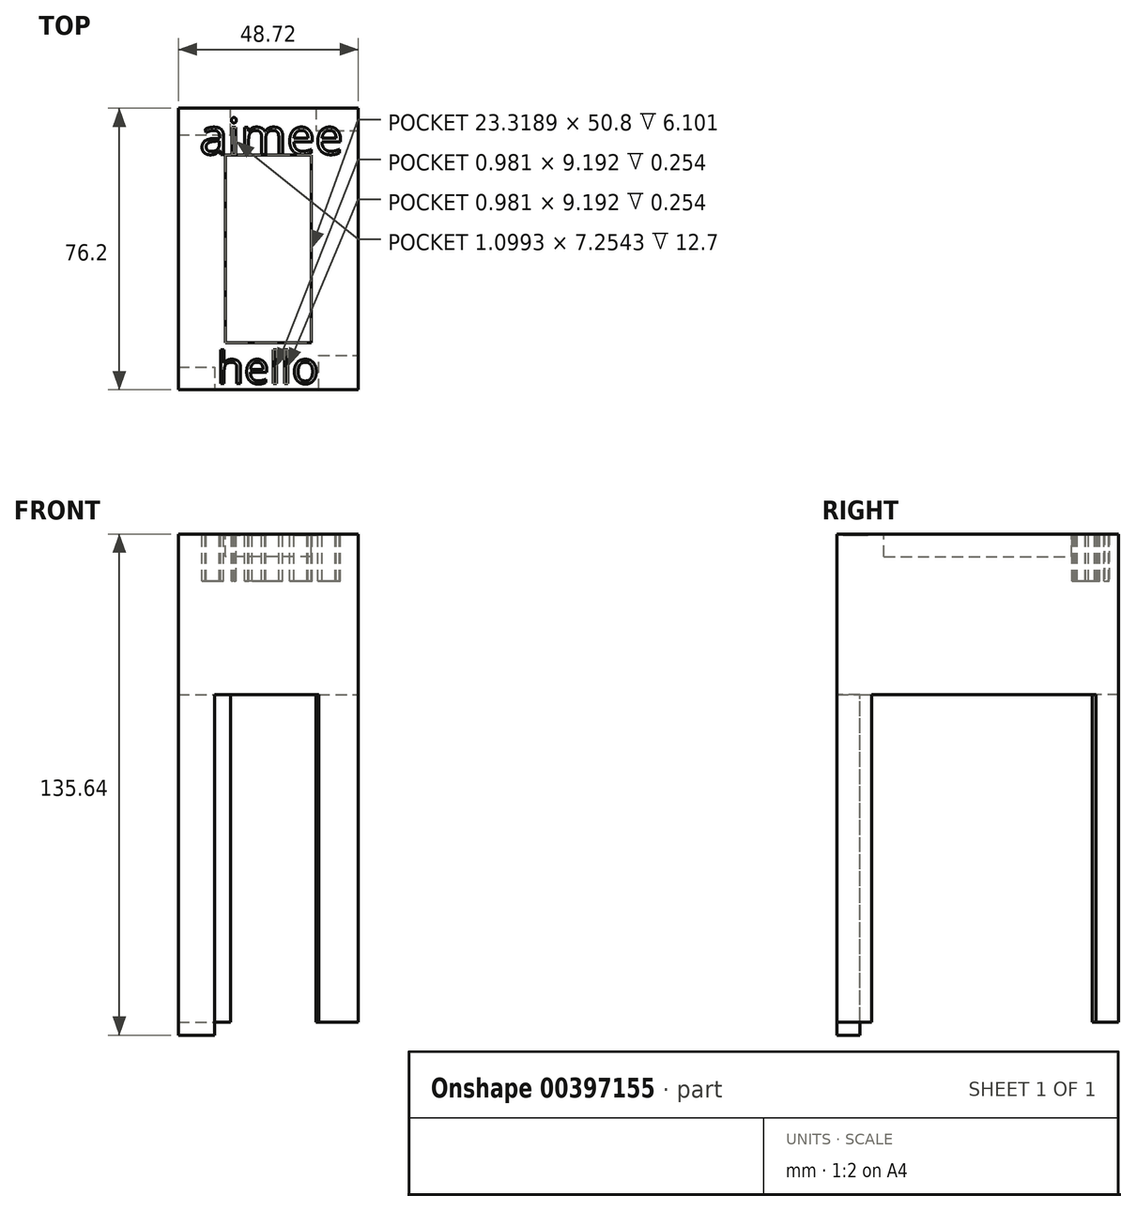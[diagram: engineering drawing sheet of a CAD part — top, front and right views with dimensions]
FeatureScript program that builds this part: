
annotation { "Feature Type Name" : "Feature", "Feature Type Description" : "" }
export const myFeature = defineFeature(function(context is Context, id is Id, definition is map)
    precondition{}
    {
        {
            var Q0;
            Q0=qCreatedBy(makeId("Front.planeOp"),FACE);
            var sketch = newSketch(context, id + "F0", { "sketchPlane" : qUnion([Q0])});
            skLineSegment(sketch, "E0.bottom", {"start": v(-31.88, 2.44) * mm, "end": v(16.84, 2.44) * mm});
            skLineSegment(sketch, "E0.top", {"start": v(-31.88, 45.88) * mm, "end": v(16.84, 45.88) * mm});
            skLineSegment(sketch, "E0.left", {"start": v(-31.88, 2.44) * mm, "end": v(-31.88, 45.88) * mm});
            skLineSegment(sketch, "E0.right", {"start": v(16.84, 2.44) * mm, "end": v(16.84, 45.88) * mm});
            skSolve(sketch);
        }
        {
            var Q0;
            Q0=makeQuery(id+"F0.imprint","IMPRINT",FACE,{"disambiguationData":[TD([[makeQuery(id+"F0.imprint","IMPRINT",EDGE,{"derivedFrom":sQuery(id+"F0.wireOp",EDGE,"E0.bottom")}),1.0]])]});
            extrude(context, id + "F1", {"entities" : qUnion([Q0]), "depth" : 76.2 * mm});
        }
        {
            var Q0;
            Q0=makeQuery(id+"F1.opExtrude","SWEPT_FACE",FACE,{"disambiguationData":[OSD([sQuery(id+"F0.wireOp",EDGE,"E0.top")])]});
            shell(context, id + "F2", {"entities" : qUnion([Q0]), "thickness" : 12.7 * mm});
        }
        {
            var Q0;
            Q0=makeQuery(id+"F1.opExtrude","CAP_FACE",FACE,{"disambiguationData":[OSD([sQuery(id+"F0.wireOp",EDGE,"E0.bottom"),sQuery(id+"F0.wireOp",EDGE,"E0.top"),sQuery(id+"F0.wireOp",EDGE,"E0.left"),sQuery(id+"F0.wireOp",EDGE,"E0.right")])],"isStart":false});
            var Q1;
            Q1=makeQuery(id+"F1.opExtrude","SWEPT_FACE",FACE,{"disambiguationData":[OSD([sQuery(id+"F0.wireOp",EDGE,"E0.right")])]});
            var Q2;
            Q2=makeQuery(id+"F1.opExtrude","SWEPT_FACE",FACE,{"disambiguationData":[OSD([sQuery(id+"F0.wireOp",EDGE,"E0.left")])]});
            shell(context, id + "F3", {"entities" : qUnion([Q0, Q1, Q2]), "thickness" : 2.54 * mm});
        }
        {
            var Q0;
            Q0=makeQuery(id+"F1.opExtrude","SWEPT_FACE",FACE,{"disambiguationData":[OSD([sQuery(id+"F0.wireOp",EDGE,"E0.bottom")])]});
            var sketch = newSketch(context, id + "F4", { "sketchPlane" : qUnion([Q0])});
            skLineSegment(sketch, "E1.bottom", {"start": v(-31.88, 69.99) * mm, "end": v(-22.12, 69.99) * mm});
            skLineSegment(sketch, "E1.top", {"start": v(-31.88, 76.2) * mm, "end": v(-22.12, 76.2) * mm});
            skLineSegment(sketch, "E1.left", {"start": v(-31.88, 69.99) * mm, "end": v(-31.88, 76.2) * mm});
            skLineSegment(sketch, "E1.right", {"start": v(-22.12, 69.99) * mm, "end": v(-22.12, 76.2) * mm});
            skSolve(sketch);
        }
        {
            var Q0;
            Q0=makeQuery(id+"F4.imprint","IMPRINT",FACE,{"disambiguationData":[TD([[makeQuery(id+"F4.imprint","IMPRINT",EDGE,{"derivedFrom":sQuery(id+"F4.wireOp",EDGE,"E1.bottom")}),1.0]])]});
            extrude(context, id + "F5", {"entities" : qUnion([Q0]), "operationType" : NewBodyOperationType.ADD, "depth" : 92.2 * mm});
        }
        {
            var Q0;
            Q0=makeQuery(id+"F1.opExtrude","SWEPT_FACE",FACE,{"disambiguationData":[OSD([sQuery(id+"F0.wireOp",EDGE,"E0.bottom")])]});
            var sketch = newSketch(context, id + "F6", { "sketchPlane" : qUnion([Q0])});
            skLineSegment(sketch, "E2.bottom", {"start": v(6.1, 76.2) * mm, "end": v(16.84, 76.2) * mm});
            skLineSegment(sketch, "E2.top", {"start": v(6.1, 66.82) * mm, "end": v(16.84, 66.82) * mm});
            skLineSegment(sketch, "E2.left", {"start": v(6.1, 76.2) * mm, "end": v(6.1, 66.82) * mm});
            skLineSegment(sketch, "E2.right", {"start": v(16.84, 76.2) * mm, "end": v(16.84, 66.82) * mm});
            skSolve(sketch);
        }
        {
            var Q0;
            Q0=makeQuery(id+"F6.imprint","IMPRINT",FACE,{"disambiguationData":[TD([[makeQuery(id+"F6.imprint","IMPRINT",EDGE,{"derivedFrom":sQuery(id+"F6.wireOp",EDGE,"E2.bottom")}),-1.0]])]});
            extrude(context, id + "F7", {"entities" : qUnion([Q0]), "operationType" : NewBodyOperationType.ADD, "depth" : 88.65 * mm});
        }
        {
            var Q0;
            Q0=makeQuery(id+"F1.opExtrude","SWEPT_FACE",FACE,{"disambiguationData":[OSD([sQuery(id+"F0.wireOp",EDGE,"E0.bottom")])]});
            var sketch = newSketch(context, id + "F8", { "sketchPlane" : qUnion([Q0])});
            skLineSegment(sketch, "E3.bottom", {"start": v(-31.88, 7.16) * mm, "end": v(-17.79, 7.16) * mm});
            skLineSegment(sketch, "E3.top", {"start": v(-31.88, 0) * mm, "end": v(-17.79, 0) * mm});
            skLineSegment(sketch, "E3.left", {"start": v(-31.88, 7.16) * mm, "end": v(-31.88, 0) * mm});
            skLineSegment(sketch, "E3.right", {"start": v(-17.79, 7.16) * mm, "end": v(-17.79, 0) * mm});
            skLineSegment(sketch, "E4.bottom", {"start": v(5.33, 0) * mm, "end": v(16.84, 0) * mm});
            skLineSegment(sketch, "E4.top", {"start": v(5.33, 6.1) * mm, "end": v(16.84, 6.1) * mm});
            skLineSegment(sketch, "E4.left", {"start": v(5.33, 0) * mm, "end": v(5.33, 6.1) * mm});
            skLineSegment(sketch, "E4.right", {"start": v(16.84, 0) * mm, "end": v(16.84, 6.1) * mm});
            skSolve(sketch);
        }
        {
            var Q0;
            Q0=makeQuery(id+"F8.imprint","IMPRINT",FACE,{"disambiguationData":[TD([[makeQuery(id+"F8.imprint","IMPRINT",EDGE,{"derivedFrom":sQuery(id+"F8.wireOp",EDGE,"E3.bottom")}),-1.0]])]});
            var Q1;
            Q1=makeQuery(id+"F8.imprint","IMPRINT",FACE,{"disambiguationData":[TD([[makeQuery(id+"F8.imprint","IMPRINT",EDGE,{"derivedFrom":sQuery(id+"F8.wireOp",EDGE,"E4.bottom")}),1.0]])]});
            extrude(context, id + "F9", {"entities" : qUnion([Q0, Q1]), "operationType" : NewBodyOperationType.ADD, "depth" : 56.4 * mm});
        }
        {
            var Q0;
            Q0=makeQuery(id+"F9.opExtrude","CAP_FACE",FACE,{"disambiguationData":[OSD([sQuery(id+"F8.wireOp",EDGE,"E3.bottom"),sQuery(id+"F8.wireOp",EDGE,"E3.top"),sQuery(id+"F8.wireOp",EDGE,"E3.left"),sQuery(id+"F8.wireOp",EDGE,"E3.right")])],"isStart":false});
            var Q1;
            Q1=makeQuery(id+"F9.opExtrude","CAP_FACE",FACE,{"disambiguationData":[OSD([sQuery(id+"F8.wireOp",EDGE,"E4.bottom"),sQuery(id+"F8.wireOp",EDGE,"E4.top"),sQuery(id+"F8.wireOp",EDGE,"E4.left"),sQuery(id+"F8.wireOp",EDGE,"E4.right")])],"isStart":false});
            var Q2;
            Q2=makeQuery(id+"F7.opExtrude","CAP_FACE",FACE,{"disambiguationData":[OSD([sQuery(id+"F6.wireOp",EDGE,"E2.bottom"),sQuery(id+"F6.wireOp",EDGE,"E2.top"),sQuery(id+"F6.wireOp",EDGE,"E2.left"),sQuery(id+"F6.wireOp",EDGE,"E2.right")])],"isStart":false});
            extrude(context, id + "F10", {"entities" : qUnion([Q0, Q1]), "operationType" : NewBodyOperationType.ADD, "endBound" : BoundingType.UP_TO_SURFACE, "endBoundEntityFace" : qUnion([Q2]), "depth" : mm});
        }
        {
            var Q0;
            {var subQ0=sQuery(id+"F0.wireOp",EDGE,"E0.bottom");Q0=makeQuery(id+"F3.opShell","OFFSET_FACE",FACE,{"disambiguationData":[OSD([subQ0]),TDD([makeQuery(id+"F1.opExtrude","SWEPT_FACE",FACE,{"disambiguationData":[OSD([subQ0])]})])]});}
            var sketch = newSketch(context, id + "F11", { "sketchPlane" : qUnion([Q0])});
            skLineSegment(sketch, "E5.bottom", {"start": v(16.84, -76.2) * mm, "end": v(5.2, -76.2) * mm});
            skLineSegment(sketch, "E5.top", {"start": v(16.84, -63.84) * mm, "end": v(5.2, -63.84) * mm});
            skLineSegment(sketch, "E5.left", {"start": v(16.84, -76.2) * mm, "end": v(16.84, -63.84) * mm});
            skLineSegment(sketch, "E5.right", {"start": v(5.2, -76.2) * mm, "end": v(5.2, -63.84) * mm});
            skLineSegment(sketch, "E6.bottom", {"start": v(16.84, -13.65) * mm, "end": v(5.85, -13.65) * mm});
            skLineSegment(sketch, "E6.top", {"start": v(16.84, -2.54) * mm, "end": v(5.85, -2.54) * mm});
            skLineSegment(sketch, "E6.left", {"start": v(16.84, -13.65) * mm, "end": v(16.84, -2.54) * mm});
            skLineSegment(sketch, "E6.right", {"start": v(5.85, -13.65) * mm, "end": v(5.85, -2.54) * mm});
            skLineSegment(sketch, "E7.bottom", {"start": v(-31.88, -63.84) * mm, "end": v(-18.49, -63.84) * mm});
            skLineSegment(sketch, "E7.top", {"start": v(-31.88, -76.2) * mm, "end": v(-18.49, -76.2) * mm});
            skLineSegment(sketch, "E7.left", {"start": v(-31.88, -63.84) * mm, "end": v(-31.88, -76.2) * mm});
            skLineSegment(sketch, "E7.right", {"start": v(-18.49, -63.84) * mm, "end": v(-18.49, -76.2) * mm});
            skSolve(sketch);
        }
        {
            var Q0;
            Q0=makeQuery(id+"F11.imprint","IMPRINT",FACE,{"disambiguationData":[TD([[makeQuery(id+"F11.imprint","IMPRINT",EDGE,{"derivedFrom":sQuery(id+"F11.wireOp",EDGE,"E5.bottom")}),1.0]])]});
            var Q1;
            Q1=makeQuery(id+"F11.imprint","IMPRINT",FACE,{"disambiguationData":[TD([[makeQuery(id+"F11.imprint","IMPRINT",EDGE,{"derivedFrom":sQuery(id+"F11.wireOp",EDGE,"E6.bottom")}),-1.0]])]});
            var Q2;
            {var subQ10=sQuery(id+"F11.wireOp",EDGE,"E5.top");Q2=makeQuery(id+"F11.imprint","IMPRINT",FACE,{"disambiguationData":[TD([[makeQuery(id+"F11.imprint","IMPRINT",EDGE,{"derivedFrom":subQ10}),-1.0]])]});}
            var Q3;
            Q3=makeQuery(id+"F11.imprint","IMPRINT",FACE,{"disambiguationData":[TD([[makeQuery(id+"F11.imprint","IMPRINT",EDGE,{"derivedFrom":sQuery(id+"F11.wireOp",EDGE,"E7.bottom")}),-1.0]])]});
            extrude(context, id + "F12", {"entities" : qUnion([Q0, Q1, Q2, Q3]), "operationType" : NewBodyOperationType.ADD, "depth" : 34.8 * mm});
        }
        {
            var Q0;
            Q0=makeQuery(id+"F1.opExtrude","SWEPT_FACE",FACE,{"disambiguationData":[OSD([sQuery(id+"F0.wireOp",EDGE,"E0.top")])]});
            var sketch = newSketch(context, id + "F13", { "sketchPlane" : qUnion([Q0])});
            skSolve(sketch);
        }
        {
            var Q0;
            {var subQ0=sQuery(id+"F0.wireOp",EDGE,"E0.top");var subQ2=makeQuery(id+"F1.opExtrude","CAP_EDGE",EDGE,{"disambiguationData":[OSD([subQ0])],"isStart":true});Q0=makeQuery(id+"F13.imprint","IMPRINT",FACE,{"disambiguationData":[TD([[makeQuery(id+"F13.imprint","IMPRINT",EDGE,{"derivedFrom":subQ2}),-1.0]])]});}
            extrude(context, id + "F14", {"entities" : qUnion([Q0]), "operationType" : NewBodyOperationType.ADD, "oppositeDirection" : true, "depth" : 25.4 * mm});
        }
        {
            var Q0;
            Q0=makeQuery(id+"F1.opExtrude","SWEPT_FACE",FACE,{"disambiguationData":[OSD([sQuery(id+"F0.wireOp",EDGE,"E0.top")])]});
            var sketch = newSketch(context, id + "F15", { "sketchPlane" : qUnion([Q0])});
            skText(sketch, "E8", { "text": "hello", "fontName": "OpenSans-Regular.ttf"});
            const initialGuessF15  = {"E8": [-0.0215, -0.0745, 1, 0, 0.00871]};
            skSetInitialGuess(sketch, initialGuessF15);
            skSolve(sketch);
        }
        {
            var Q0;
            Q0 = qSketchRegion(id + "F15", true);
            extrude(context, id + "F16", {"entities" : qUnion([Q0]), "operationType" : NewBodyOperationType.REMOVE, "oppositeDirection" : true, "depth" : 0.25 * mm});
        }
        {
            var Q0;
            {var subQ3=sQuery(id+"F0.wireOp",EDGE,"E0.top");var subQ5=sQuery(id+"F0.wireOp",EDGE,"E0.left");Q0=makeQuery(id+"F16.boolean.opBoolean","SPLIT",FACE,{"disambiguationData":[TD([makeQuery(id+"F1.opExtrude","SWEPT_FACE",FACE,{"disambiguationData":[OSD([subQ5])]})])],"derivedFrom":makeQuery(id+"F1.opExtrude","SWEPT_FACE",FACE,{"disambiguationData":[OSD([subQ3])]})});}
            var sketch = newSketch(context, id + "F17", { "sketchPlane" : qUnion([Q0])});
            skSolve(sketch);
        }
        {
            var Q0;
            {var subQ0=sQuery(id+"F0.wireOp",EDGE,"E0.top");var subQ2=makeQuery(id+"F1.opExtrude","CAP_EDGE",EDGE,{"disambiguationData":[OSD([subQ0])],"isStart":true});Q0=makeQuery(id+"F17.imprint","IMPRINT",FACE,{"disambiguationData":[TD([[makeQuery(id+"F17.imprint","IMPRINT",EDGE,{"derivedFrom":subQ2}),-1.0]])]});}
            var sketch = newSketch(context, id + "F18", { "sketchPlane" : qUnion([Q0])});
            skText(sketch, "E9", { "text": "aimee", "fontName": "OpenSans-Regular.ttf"});
            const initialGuessF18  = {"E9": [-0.0261, -0.01245, 1, 0, 0.00976]};
            skSetInitialGuess(sketch, initialGuessF18);
            skSolve(sketch);
        }
        {
            var Q0;
            Q0 = qSketchRegion(id + "F18", true);
            extrude(context, id + "F19", {"entities" : qUnion([Q0]), "operationType" : NewBodyOperationType.REMOVE, "oppositeDirection" : true, "depth" : 12.7 * mm});
        }
    });
